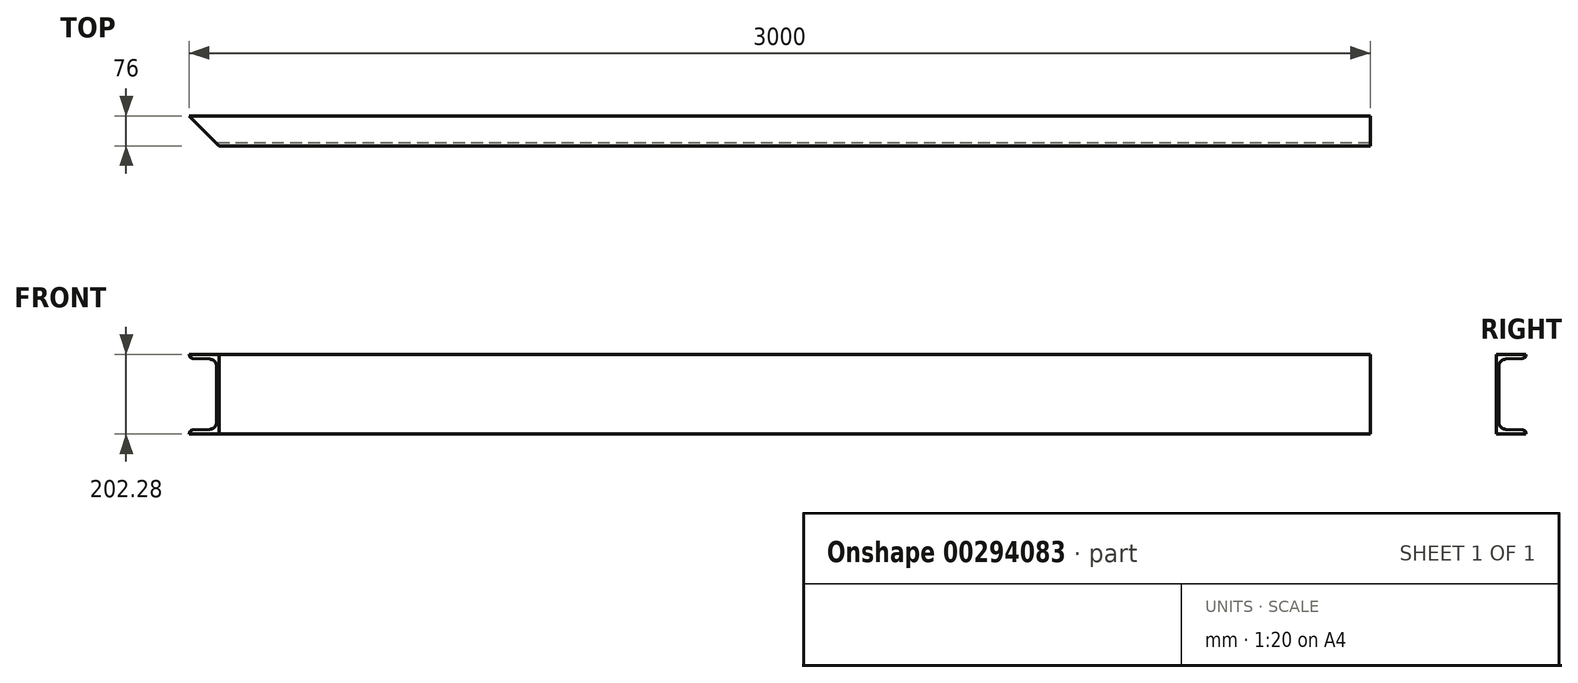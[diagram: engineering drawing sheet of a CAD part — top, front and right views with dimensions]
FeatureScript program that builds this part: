
annotation { "Feature Type Name" : "Feature", "Feature Type Description" : "" }
export const myFeature = defineFeature(function(context is Context, id is Id, definition is map)
    precondition{}
    {
        {
            var Q0;
            Q0=qCreatedBy(makeId("Right.planeOp"),FACE);
            var sketch = newSketch(context, id + "F0", { "sketchPlane" : qUnion([Q0])});
            skLineSegment(sketch, "E0", {"start": v(0, 0) * mm, "end": v(0, 203) * mm});
            skLineSegment(sketch, "E1", {"start": v(0, 203) * mm, "end": v(76, 203) * mm});
            skLineSegment(sketch, "E2", {"start": v(76, 203) * mm, "end": v(76, 201.67) * mm});
            skLineSegment(sketch, "E3", {"start": v(7.1, 173.86) * mm, "end": v(7.1, 29.86) * mm});
            skLineSegment(sketch, "E4", {"start": v(41.55, 191.8) * mm, "end": v(41.55, 278.39) * mm, "construction": true});
            skLineSegment(sketch, "E5", {"start": v(23.21, 190.84) * mm, "end": v(67.94, 193.18) * mm});
            skPoint(sketch, "E6.orphan", {"position": v(76, 193.47) * mm});
            skPoint(sketch, "E7.visualSharp", {"position": v(7.1, 190) * mm});
            skArc(sketch, "E7.filletArc", {"start": v(23.21, 190.84) * mm, "mid": v(11.77, 185.56) * mm, "end": v(7.1, 173.86) * mm});
            skPoint(sketch, "E8.visualSharp", {"position": v(76, 193.6) * mm});
            skArc(sketch, "E8.filletArc", {"start": v(67.94, 193.18) * mm, "mid": v(73.67, 195.82) * mm, "end": v(76, 201.67) * mm});
            skLineSegment(sketch, "E9", {"start": v(7.1, 101.86) * mm, "end": v(142.57, 101.86) * mm, "construction": true});
            skLineSegment(sketch, "E10.MirrorCS", {"start": v(76, 0.72) * mm, "end": v(76, 2.05) * mm});
            skArc(sketch, "E11.MirrorCS", {"start": v(67.94, 10.54) * mm, "mid": v(73.67, 7.9) * mm, "end": v(76, 2.05) * mm});
            skLineSegment(sketch, "E12.MirrorCS", {"start": v(23.21, 12.89) * mm, "end": v(67.94, 10.54) * mm});
            skLineSegment(sketch, "E13.MirrorCS", {"start": v(0, 0.72) * mm, "end": v(76, 0.72) * mm});
            skPoint(sketch, "E14.MirrorP", {"position": v(76, 10.12) * mm});
            skPoint(sketch, "E15.MirrorP", {"position": v(7.1, 13.73) * mm});
            skArc(sketch, "E16.MirrorCS", {"start": v(23.21, 12.89) * mm, "mid": v(11.77, 18.16) * mm, "end": v(7.1, 29.86) * mm});
            skPoint(sketch, "E17.MirrorP", {"position": v(76, 10.26) * mm});
            skSolve(sketch);
        }
        {
            var Q0;
            Q0=qSketchRegion(id+"F0",true);
            extrude(context, id + "F1", {"entities" : qUnion([Q0]), "depth" : 3000 * mm});
        }
        {
            var Q0;
            Q0=qCreatedBy(makeId("Top.planeOp"),FACE);
            var sketch = newSketch(context, id + "F2", { "sketchPlane" : qUnion([Q0])});
            skLineSegment(sketch, "E18.bottom", {"start": v(0, 0) * mm, "end": v(76, 0) * mm});
            skLineSegment(sketch, "E18.left", {"start": v(0, 0) * mm, "end": v(0, 76) * mm});
            skLineSegment(sketch, "E19", {"start": v(0, 76) * mm, "end": v(76, 0) * mm});
            skSolve(sketch);
        }
        {
            var Q0;
            Q0 = qSketchRegion(id + "F2", true);
            extrude(context, id + "F3", {"entities" : qUnion([Q0]), "operationType" : NewBodyOperationType.REMOVE, "endBound" : BoundingType.THROUGH_ALL, "depth" : 25 * mm});
        }
        {
            var Q0;
            Q0=qCreatedBy(makeId("Right.planeOp"),FACE);
            cPlane(context, id + "F4", {"entities" : qUnion([Q0]), "cplaneType" : CPlaneType.OFFSET, "offset" : (3000 / 2) * mm, "width" : 150 * mm, "height" : 150 * mm});
        }
    });
